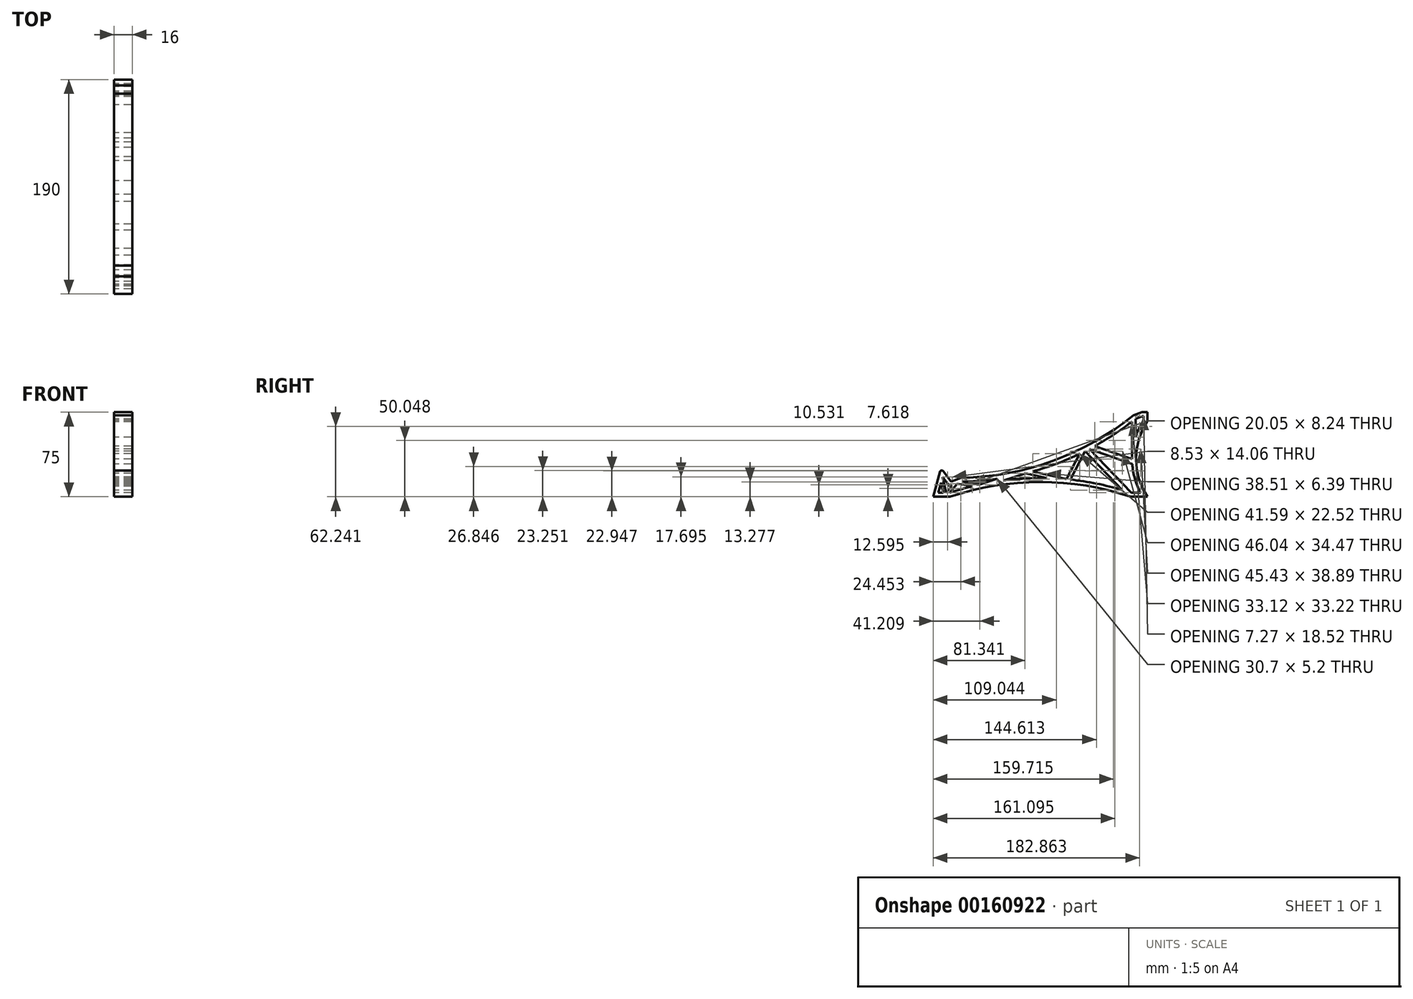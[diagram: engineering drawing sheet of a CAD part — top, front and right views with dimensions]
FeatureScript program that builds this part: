
annotation { "Feature Type Name" : "Feature", "Feature Type Description" : "" }
export const myFeature = defineFeature(function(context is Context, id is Id, definition is map)
    precondition{}
    {
        {
            var Q0;
            Q0=qCreatedBy(makeId("Right.planeOp"),FACE);
            var sketch = newSketch(context, id + "F0", { "sketchPlane" : qUnion([Q0])});
            skArc(sketch, "E0", {"start": v(175, 0) * mm, "mid": v(95, 13.15) * mm, "end": v(15, 0) * mm});
            skLineSegment(sketch, "E1", {"start": v(15, 0) * mm, "end": v(0, 0) * mm});
            skLineSegment(sketch, "E2", {"start": v(175, 0) * mm, "end": v(190, 0) * mm});
            skArc(sketch, "E3", {"start": v(190, 67) * mm, "mid": v(179.78, 33.5) * mm, "end": v(190, 0) * mm});
            skArc(sketch, "E4", {"start": v(25.2, 16.84) * mm, "mid": v(105.96, 31.87) * mm, "end": v(177.48, 72.26) * mm});
            skLineSegment(sketch, "E5", {"start": v(190, 67) * mm, "end": v(190, 75) * mm});
            skLineSegment(sketch, "E6", {"start": v(177.48, 72.26) * mm, "end": v(185, 75) * mm});
            skLineSegment(sketch, "E7", {"start": v(185, 75) * mm, "end": v(190, 75) * mm});
            skLineSegment(sketch, "E8", {"start": v(25.2, 16.84) * mm, "end": v(15.81, 13.42) * mm});
            skLineSegment(sketch, "E9", {"start": v(25.2, 16.84) * mm, "end": v(177.48, 72.26) * mm, "construction": true});
            skLineSegment(sketch, "E10", {"start": v(6.81, 25.42) * mm, "end": v(0, 0) * mm});
            skLineSegment(sketch, "E11", {"start": v(6.81, 25.42) * mm, "end": v(15.81, 13.42) * mm});
            skArc(sketch, "E12.0", {"start": v(186.5, 68.05) * mm, "mid": v(176.33, 36.14) * mm, "end": v(183.81, 3.5) * mm});
            skLineSegment(sketch, "E12.1", {"start": v(175.57, 3.5) * mm, "end": v(183.81, 3.5) * mm});
            skArc(sketch, "E12.2", {"start": v(175.57, 3.5) * mm, "mid": v(95, 16.65) * mm, "end": v(14.43, 3.5) * mm});
            skLineSegment(sketch, "E12.3", {"start": v(14.43, 3.5) * mm, "end": v(4.56, 3.5) * mm});
            skLineSegment(sketch, "E12.4", {"start": v(8.33, 17.56) * mm, "end": v(4.56, 3.5) * mm});
            skLineSegment(sketch, "E12.5", {"start": v(186.5, 68.05) * mm, "end": v(186.5, 71.5) * mm});
            skLineSegment(sketch, "E12.6", {"start": v(185.62, 71.5) * mm, "end": v(186.5, 71.5) * mm});
            skLineSegment(sketch, "E12.7", {"start": v(179.23, 69.17) * mm, "end": v(185.62, 71.5) * mm});
            skArc(sketch, "E12.8", {"start": v(25.86, 13.35) * mm, "mid": v(107.16, 28.58) * mm, "end": v(179.23, 69.17) * mm});
            skLineSegment(sketch, "E12.9", {"start": v(25.86, 13.35) * mm, "end": v(14.57, 9.24) * mm});
            skLineSegment(sketch, "E12.10", {"start": v(8.33, 17.56) * mm, "end": v(14.57, 9.24) * mm});
            skLineSegment(sketch, "E13", {"start": v(179.23, 69.17) * mm, "end": v(179.34, 52.98) * mm});
            skLineSegment(sketch, "E14", {"start": v(176.28, 33.44) * mm, "end": v(176.04, 66.66) * mm});
            skLineSegment(sketch, "E15", {"start": v(143.15, 44.97) * mm, "end": v(176.28, 33.44) * mm});
            skLineSegment(sketch, "E16", {"start": v(138.38, 42.4) * mm, "end": v(176.43, 29.15) * mm});
            skLineSegment(sketch, "E17", {"start": v(175.57, 3.5) * mm, "end": v(138.38, 42.4) * mm});
            skLineSegment(sketch, "E18", {"start": v(134.67, 40.48) * mm, "end": v(167.63, 6.02) * mm});
            skLineSegment(sketch, "E19", {"start": v(134.67, 40.48) * mm, "end": v(121.6, 15.25) * mm});
            skLineSegment(sketch, "E20", {"start": v(129.84, 38.1) * mm, "end": v(118.17, 15.58) * mm});
            skLineSegment(sketch, "E21", {"start": v(118.17, 15.58) * mm, "end": v(88.25, 22.53) * mm});
            skLineSegment(sketch, "E22", {"start": v(82.04, 20.9) * mm, "end": v(100.6, 16.58) * mm});
            skLineSegment(sketch, "E23", {"start": v(82.04, 20.9) * mm, "end": v(62.09, 14.5) * mm});
            skLineSegment(sketch, "E24", {"start": v(56.56, 15.88) * mm, "end": v(40.3, 10.68) * mm});
            skLineSegment(sketch, "E25", {"start": v(25.86, 13.35) * mm, "end": v(40.3, 10.68) * mm});
            skLineSegment(sketch, "E26", {"start": v(21.42, 11.74) * mm, "end": v(34.48, 9.32) * mm});
            skLineSegment(sketch, "E27", {"start": v(21.42, 11.74) * mm, "end": v(14.43, 3.5) * mm});
            skLineSegment(sketch, "E28", {"start": v(16.86, 10.08) * mm, "end": v(11.28, 3.5) * mm});
            skLineSegment(sketch, "E29", {"start": v(11.28, 3.5) * mm, "end": v(8.33, 17.56) * mm});
            skLineSegment(sketch, "E30", {"start": v(6.95, 12.43) * mm, "end": v(8.83, 3.5) * mm});
            skSolve(sketch);
        }
        {
            var Q0;
            Q0=makeQuery(id+"F0.imprint","IMPRINT",FACE,{"disambiguationData":[TD([[makeQuery(id+"F0.imprint","IMPRINT",EDGE,{"derivedFrom":sQuery(id+"F0.wireOp",EDGE,"E0")}),-1.0]])]});
            var Q1;
            {var subQ0=sQuery(id+"F0.wireOp",EDGE,"E29");Q1=makeQuery(id+"F0.imprint","IMPRINT",FACE,{"disambiguationData":[TD([[makeQuery(id+"F0.imprint","IMPRINT",EDGE,{"derivedFrom":subQ0}),1.0]])]});}
            var Q2;
            {var subQ0=sQuery(id+"F0.wireOp",EDGE,"E27");Q2=makeQuery(id+"F0.imprint","IMPRINT",FACE,{"disambiguationData":[TD([[makeQuery(id+"F0.imprint","IMPRINT",EDGE,{"derivedFrom":subQ0}),-1.0]])]});}
            var Q3;
            {var subQ0=sQuery(id+"F0.wireOp",EDGE,"E25");Q3=makeQuery(id+"F0.imprint","IMPRINT",FACE,{"disambiguationData":[TD([[makeQuery(id+"F0.imprint","IMPRINT",EDGE,{"derivedFrom":subQ0}),-1.0]])]});}
            var Q4;
            {var subQ0=sQuery(id+"F0.wireOp",EDGE,"E21");Q4=makeQuery(id+"F0.imprint","IMPRINT",FACE,{"disambiguationData":[TD([[makeQuery(id+"F0.imprint","IMPRINT",EDGE,{"derivedFrom":subQ0}),1.0]])]});}
            var Q5;
            {var subQ0=sQuery(id+"F0.wireOp",EDGE,"E19");Q5=makeQuery(id+"F0.imprint","IMPRINT",FACE,{"disambiguationData":[TD([[makeQuery(id+"F0.imprint","IMPRINT",EDGE,{"derivedFrom":subQ0}),-1.0]])]});}
            var Q6;
            {var subQ0=sQuery(id+"F0.wireOp",EDGE,"E17");Q6=makeQuery(id+"F0.imprint","IMPRINT",FACE,{"disambiguationData":[TD([[makeQuery(id+"F0.imprint","IMPRINT",EDGE,{"derivedFrom":subQ0}),1.0]])]});}
            var Q7;
            {var subQ0=sQuery(id+"F0.wireOp",EDGE,"E15");Q7=makeQuery(id+"F0.imprint","IMPRINT",FACE,{"disambiguationData":[TD([[makeQuery(id+"F0.imprint","IMPRINT",EDGE,{"derivedFrom":subQ0}),-1.0]])]});}
            var Q8;
            {var subQ0=sQuery(id+"F0.wireOp",EDGE,"E13");Q8=makeQuery(id+"F0.imprint","IMPRINT",FACE,{"disambiguationData":[TD([[makeQuery(id+"F0.imprint","IMPRINT",EDGE,{"derivedFrom":subQ0}),-1.0]])]});}
            var Q9;
            {var subQ0=sQuery(id+"F0.wireOp",EDGE,"E23");Q9=makeQuery(id+"F0.imprint","IMPRINT",FACE,{"disambiguationData":[TD([[makeQuery(id+"F0.imprint","IMPRINT",EDGE,{"derivedFrom":subQ0}),-1.0]])]});}
            extrude(context, id + "F1", {"entities" : qUnion([Q0, Q1, Q2, Q3, Q4, Q5, Q6, Q7, Q8, Q9]), "depth" : 16 * mm});
        }
        {
            var Q0;
            Q0=makeQuery(id+"F1.opExtrude","SWEPT_EDGE",EDGE,{"disambiguationData":[OSD([sQuery(id+"F0.wireOp",EDGE,"E10"),sQuery(id+"F0.wireOp",EDGE,"E11")])]});
            fillet(context, id + "F2", {"entities" : qUnion([Q0]), "radius" : 1.6 * mm, "tangentPropagation" : true, "allowEdgeOverflow" : false});
        }
    });
